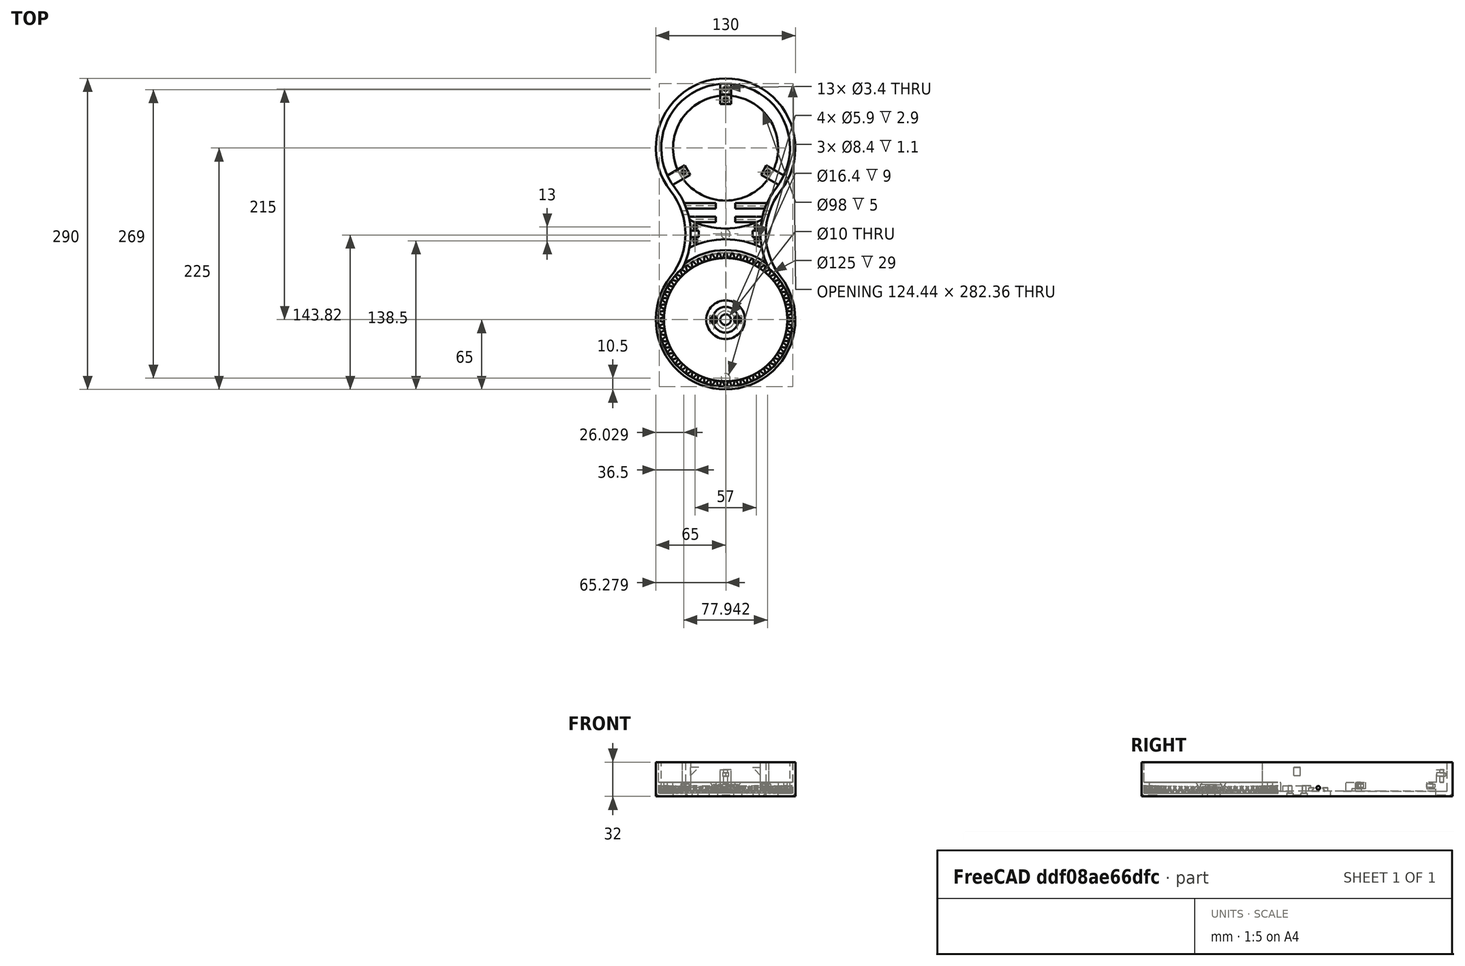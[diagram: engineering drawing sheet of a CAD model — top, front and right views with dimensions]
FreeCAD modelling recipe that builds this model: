
FCSTD DOCUMENT  (FreeCAD 0.19R24276 (Git))
Label: Art2BodyA
License: All rights reserved
LicenseURL: http://en.wikipedia.org/wiki/All_rights_reserved
objects: Sketcher::SketchObject×22, PartDesign::Pocket×15, PartDesign::Line×11, PartDesign::CoordinateSystem×10, PartDesign::Pad×7, PartDesign::Plane×4, PartDesign::Body×2, Spreadsheet::Sheet×1, Part::FeaturePython×1, Part::Cylinder×1, Part::Cut×1, Part::MultiFuse×1, PartDesign::FeatureBase×1, PartDesign::Chamfer×1, PartDesign::Mirrored×1, PartDesign::PolarPattern×1, PartDesign::Fillet×1
note: 104 computed .brp shape members not serialized (recipe doc carries the construction recipe); baked Part::Feature solids carry a one-line shape summary decoded from their .brp

FEATURE [Spreadsheet::Sheet] Spreadsheet
  cells = A2=M3BoltBodyRadius; B2(M3BoltBodyRadius)=1.7; A3=M3BoltHeadRadius; B3(M3BoltHeadRadius)=2.95; A4=M3NutCircumradius; B4(M3NutCircumradius)=3.35; A5=M3NutThickness; B5(M3NutThickness)=3; A6=Bearing655ZZBodyRadius; B6(Bearing655ZZBodyRadius)=8.199999999999999; A7=MagnetRadius; B7(MagnetRadius)=4.2; A8=MagnetThickness; B8(MagnetThickness)=1.1
FEATURE [Sketcher::SketchObject] Sketch
  FullyConstrained = true
  MapMode = 5
  Support = -> [XY_Plane]
  sketch-geometry (4):
    g0: ArcOfCircle CenterX=0 CenterY=0 CenterZ=0 NormalX=0 NormalY=0 NormalZ=1 AngleXU=0 Radius=65 StartAngle=2.47872 EndAngle=6.94606
    g1: ArcOfCircle CenterX=102.47 CenterY=80 CenterZ=0 NormalX=0 NormalY=0 NormalZ=1 AngleXU=0 Radius=65 StartAngle=2.47872 EndAngle=3.80447
    g2: ArcOfCircle CenterX=-102.47 CenterY=80 CenterZ=0 NormalX=0 NormalY=0 NormalZ=1 AngleXU=0 Radius=65 StartAngle=5.62031 EndAngle=6.94606
    g3: ArcOfCircle CenterX=2.8e-15 CenterY=160 CenterZ=0 NormalX=0 NormalY=0 NormalZ=1 AngleXU=0 Radius=65 StartAngle=5.62031 EndAngle=10.0877
  constraints (10):
    c: Coincident(g0,g-1)
    c: Tangent(g2,g0) = 1.5708
    c: Tangent(g1,g0) = 1.5708
    c: Symmetric(g1,g2,g-2)
    c: Tangent(g3,g1) = 1.5708
    c: Tangent(g3,g2) = 1.5708
    c: Equal(g3,g0)
    c: DistanceY(g0,g3) = 160
    c: Radius(g0) = 65
    c: Equal(g2,g0)
FEATURE [PartDesign::Pad] Pad
  Direction = (1,1,1)
  Length = 32
  Length2 = 100
  Profile = -> Sketch
  Refine = true
  Type = 0
FEATURE [Sketcher::SketchObject] Sketch001
  ExternalGeometry = -> [Pad]
  FullyConstrained = true
  MapMode = 5
  Placement = pos=(0,0,32) rot=(0,0,1;0rad)
  Support = -> [Pad]
  sketch-geometry (4):
    g0: ArcOfCircle CenterX=0 CenterY=0 CenterZ=0 NormalX=0 NormalY=0 NormalZ=1 AngleXU=0 Radius=60 StartAngle=2.47872 EndAngle=6.94606
    g1: ArcOfCircle CenterX=102.47 CenterY=80 CenterZ=0 NormalX=0 NormalY=0 NormalZ=1 AngleXU=0 Radius=70 StartAngle=2.47872 EndAngle=3.80447
    g2: ArcOfCircle CenterX=-102.47 CenterY=80 CenterZ=0 NormalX=0 NormalY=0 NormalZ=1 AngleXU=0 Radius=70 StartAngle=5.62031 EndAngle=6.94606
    g3: ArcOfCircle CenterX=2.7e-15 CenterY=160 CenterZ=0 NormalX=0 NormalY=0 NormalZ=1 AngleXU=0 Radius=60 StartAngle=5.62031 EndAngle=10.0877
  constraints (9):
    c: Coincident(g0,g-1)
    c: Coincident(g1,g-4)
    c: Coincident(g2,g-5)
    c: Coincident(g2,g0)
    c: Coincident(g3,g-3)
    c: Tangent(g3,g2) = 1.5708
    c: Radius(g3) = 60
    c: Tangent(g3,g1) = 1.5708
    c: Tangent(g1,g0) = 1.5708
FEATURE [PartDesign::Pocket] Pocket
  BaseFeature = -> Pad
  Length = 27
  Length2 = 100
  Profile = -> Sketch001
  Refine = true
  Type = 0
FEATURE [Part::FeaturePython] involutegear  # WARN: FeaturePython — macro-defined, semantics opaque (R4)
  Placement = pos=(0,0,3) rot=(0,0,1;0rad)
  backlash = 0
  beta = -32
  clearance = 0.25
  double_helix = false
  dw = 120
  head = 0
  height = 15.5
  module = 2
  numpoints = 6
  pressure_angle = 20
  properties_from_tool = false
  reversed_backlash = false
  shift = 0
  simple = false
  teeth = 60
  transverse_pitch = 6.28319
  undercut = false
  version = 0.0.3
FEATURE [Sketcher::SketchObject] Sketch003
  FullyConstrained = true
  MapMode = 5
  Placement = pos=(0,0,3) rot=(0,0,1;0rad)
  sketch-geometry (1):
    g0: Circle CenterX=0 CenterY=0 CenterZ=0 NormalX=0 NormalY=0 NormalZ=1 AngleXU=0 Radius=18
  constraints (2):
    c: Coincident(g0,g-1)
    c: Radius(g0) = 18
FEATURE [PartDesign::Plane] DatumPlane
  AttachmentOffset = pos=(0,0,9) rot=(0,0,1;0rad)
  Length = 315.452
  MapMode = 5
  Placement = pos=(9,-2e-15,2e-15) rot=(0.57735,0.57735,0.57735;2.0944rad)
  ResizeMode = 0
  Support = -> [YZ_Plane001]
  Width = 82.7027
FEATURE [PartDesign::CoordinateSystem] LCS_Art2BodyA
  AttacherType = Attacher::AttachEngine3D
FEATURE [Part::Cylinder] Cylinder
  Angle = 360
  AttacherType = Attacher::AttachEngine3D
  Height = 13
  Radius = 64.9
FEATURE [Sketcher::SketchObject] Sketch021
  FullyConstrained = true
  MapMode = 5
  Placement = pos=(0,0,32) rot=(0,0,1;0rad)
  Support = -> [Pocket]
  sketch-geometry (1):
    g0: Circle CenterX=0 CenterY=0 CenterZ=0 NormalX=0 NormalY=0 NormalZ=1 AngleXU=0 Radius=62.5
  constraints (2):
    c: Coincident(g0,g-1)
    c: Radius(g0) = 62.5
FEATURE [PartDesign::Pocket] Pocket014
  BaseFeature = -> Pocket
  Length = 29
  Length2 = 100
  Profile = -> Sketch021
  Refine = true
  Type = 0
FEATURE [PartDesign::Body] Body
  Group = -> [Sketch,Pad,Sketch001,Pocket,Sketch021,Pocket014]
  Origin = -> Origin
  Tip = -> Pocket014
FEATURE [PartDesign::Plane] DatumPlane003
  AttachmentOffset = pos=(0,0,-80) rot=(0,0,1;0rad)
  Length = 147.174
  MapMode = 5
  Placement = pos=(0,80,1.78e-14) rot=(1,0,0;1.5708rad)
  ResizeMode = 0
  Support = -> [XZ_Plane001]
  Width = 74.2136
FEATURE [Part::Cut] Cut
  Base = -> Cylinder
  Refine = true
  Tool = -> involutegear
FEATURE [Part::MultiFuse] Fusion
  Refine = true
  Shapes = -> [Cut,Pocket014]
FEATURE [PartDesign::FeatureBase] BaseFeature  label="Fusion001"
  BaseFeature = -> Fusion
FEATURE [PartDesign::Pad] Pad002
  BaseFeature = -> BaseFeature
  Direction = (1,1,1)
  Length = 8
  Length2 = 100
  Profile = -> Sketch003
  Refine = true
  Type = 0
FEATURE [PartDesign::Chamfer] Chamfer
  Angle = 45
  Base = -> Pad002 [Edge755]
  BaseFeature = -> Pad002
  ChamferType = 0
  FlipDirection = false
  Refine = true
  Size = 6
  Size2 = 1
  SupportTransform = false
FEATURE [Sketcher::SketchObject] Sketch004
  FullyConstrained = true
  MapMode = 5
  Placement = pos=(0,0,11) rot=(0,0,1;0rad)
  Support = -> [Chamfer]
  expr: Constraints[5] = Spreadsheet.M3BoltBodyRadius
  sketch-geometry (3):
    g0: Circle CenterX=0 CenterY=0 CenterZ=0 NormalX=0 NormalY=0 NormalZ=1 AngleXU=0 Radius=5
    g1: Circle CenterX=11 CenterY=0 CenterZ=0 NormalX=0 NormalY=0 NormalZ=1 AngleXU=0 Radius=1.7
    g2: Circle CenterX=-11 CenterY=0 CenterZ=0 NormalX=0 NormalY=0 NormalZ=1 AngleXU=0 Radius=1.7
  constraints (7):
    c: Coincident(g0,g-1)
    c: PointOnObject(g1,g-1)
    c: Symmetric(g2,g1,g-2)
    c: DistanceX(g2,g1) = 22
    c: Radius(g0) = 5
    c: Radius(g2) = 1.7
    c: Equal(g1,g2)
FEATURE [PartDesign::Pocket] Pocket001
  BaseFeature = -> Chamfer
  Length = 5
  Length2 = 100
  Profile = -> Sketch004
  Refine = true
  Type = 1
FEATURE [Sketcher::SketchObject] Sketch005
  FullyConstrained = true
  MapMode = 5
  Placement = pos=(0,0,0) rot=(1,0,0;3.14159rad)
  Support = -> [Pocket001]
  expr: Constraints[1] = Spreadsheet.Bearing655ZZBodyRadius
  sketch-geometry (1):
    g0: Circle CenterX=0 CenterY=0 CenterZ=0 NormalX=0 NormalY=0 NormalZ=1 AngleXU=0 Radius=8.2
  constraints (2):
    c: Coincident(g0,g-1)
    c: Radius(g0) = 8.2
FEATURE [PartDesign::Pocket] Pocket002
  BaseFeature = -> Pocket001
  Length = 9
  Length2 = 100
  Profile = -> Sketch005
  Refine = true
  Type = 0
FEATURE [Sketcher::SketchObject] Sketch006
  FullyConstrained = true
  MapMode = 5
  Placement = pos=(0,0,0) rot=(1,0,0;3.14159rad)
  Support = -> [Pocket002]
  sketch-geometry (4):
    g0: LineSegment StartX=-15.3 StartY=3.5 StartZ=0 EndX=15.3 EndY=3.5 EndZ=0
    g1: LineSegment StartX=15.3 StartY=3.5 StartZ=0 EndX=15.3 EndY=-3.5 EndZ=0
    g2: LineSegment StartX=15.3 StartY=-3.5 StartZ=0 EndX=-15.3 EndY=-3.5 EndZ=0
    g3: LineSegment StartX=-15.3 StartY=-3.5 StartZ=0 EndX=-15.3 EndY=3.5 EndZ=0
  constraints (10):
    c: Coincident(g0,g1)
    c: Coincident(g1,g2)
    c: Coincident(g2,g3)
    c: Coincident(g3,g0)
    c: Horizontal(g0)
    c: Vertical(g3)
    c: Symmetric(g0,g1,g-1)
    c: Symmetric(g2,g1,g-2)
    c: DistanceX(g2,g2) = 30.6
    c: DistanceY(g3,g3) = 7
FEATURE [PartDesign::Pocket] Pocket003
  BaseFeature = -> Pocket002
  Length = 4
  Length2 = 100
  Profile = -> Sketch006
  Refine = true
  Type = 0
FEATURE [Sketcher::SketchObject] Sketch007
  ExternalGeometry = -> [Pocket003]
  FullyConstrained = true
  MapMode = 5
  Placement = pos=(0,0,11) rot=(0,0,1;0rad)
  Support = -> [Pocket003]
  expr: Constraints[39] = Spreadsheet.M3NutCircumradius
  sketch-geometry (14):
    g0: LineSegment StartX=11 StartY=3.35 StartZ=0 EndX=8.09881 EndY=1.675 EndZ=0
    g1: LineSegment StartX=8.09881 StartY=1.675 StartZ=0 EndX=8.09881 EndY=-1.675 EndZ=0
    g2: LineSegment StartX=8.09881 StartY=-1.675 StartZ=0 EndX=11 EndY=-3.35 EndZ=0
    g3: LineSegment StartX=11 StartY=-3.35 StartZ=0 EndX=13.9012 EndY=-1.675 EndZ=0
    g4: LineSegment StartX=13.9012 StartY=-1.675 StartZ=0 EndX=13.9012 EndY=1.675 EndZ=0
    g5: LineSegment StartX=13.9012 StartY=1.675 StartZ=0 EndX=11 EndY=3.35 EndZ=0
    g6: Circle CenterX=11 CenterY=0 CenterZ=0 NormalX=0 NormalY=0 NormalZ=1 AngleXU=0 Radius=3.35
    g7: LineSegment StartX=-11 StartY=3.35 StartZ=0 EndX=-13.9012 EndY=1.675 EndZ=0
    g8: LineSegment StartX=-13.9012 StartY=1.675 StartZ=0 EndX=-13.9012 EndY=-1.675 EndZ=0
    g9: LineSegment StartX=-13.9012 StartY=-1.675 StartZ=0 EndX=-11 EndY=-3.35 EndZ=0
    g10: LineSegment StartX=-11 StartY=-3.35 StartZ=0 EndX=-8.09881 EndY=-1.675 EndZ=0
    g11: LineSegment StartX=-8.09881 StartY=-1.675 StartZ=0 EndX=-8.09881 EndY=1.675 EndZ=0
    g12: LineSegment StartX=-8.09881 StartY=1.675 StartZ=0 EndX=-11 EndY=3.35 EndZ=0
    g13: Circle CenterX=-11 CenterY=0 CenterZ=0 NormalX=0 NormalY=0 NormalZ=1 AngleXU=0 Radius=3.35
  constraints (32):
    c: Coincident(g0,g1)
    c: Coincident(g1,g2)
    c: Coincident(g2,g3)
    c: Coincident(g3,g4)
    c: Coincident(g4,g5)
    c: Coincident(g5,g0)
    c: Equal(g0, g1-g5) x5
    c: PointOnObject(g0,g6)
    c: PointOnObject(g1,g6)
    c: PointOnObject(g2,g6)
    c: PointOnObject(g3,g6)
    c: PointOnObject(g4,g6)
    c: PointOnObject(g5,g6)
    c: Coincident(g6,g-3)
    c: Coincident(g7,g8)
    c: Coincident(g8,g9)
    c: Coincident(g9,g10)
    c: Coincident(g10,g11)
    c: Coincident(g11,g12)
    c: Coincident(g12,g7)
    c: Equal(g7, g8-g12) x5
    c: PointOnObject(g7,g13)
    c: PointOnObject(g8,g13)
    c: PointOnObject(g9,g13)
    c: PointOnObject(g10,g13)
    c: PointOnObject(g11,g13)
    c: PointOnObject(g12,g13)
    c: Coincident(g13,g-4)
    c: Vertical(g11)
    c: Vertical(g1)
    c: Equal(g6,g13)
    c: Radius(g6) = 3.35
FEATURE [PartDesign::Pocket] Pocket004
  BaseFeature = -> Pocket003
  Length = 4
  Length2 = 100
  Profile = -> Sketch007
  Refine = true
  Type = 0
FEATURE [Sketcher::SketchObject] Sketch008
  ExternalGeometry = -> [Pocket004]
  FullyConstrained = true
  MapMode = 5
  Placement = pos=(0,0,0) rot=(1,0,0;3.14159rad)
  Support = -> [Pocket004]
  sketch-geometry (1):
    g0: Circle CenterX=0 CenterY=-160 CenterZ=0 NormalX=0 NormalY=0 NormalZ=1 AngleXU=0 Radius=49
  constraints (2):
    c: Radius(g0) = 49
    c: Coincident(g0,g-3)
FEATURE [PartDesign::Pocket] Pocket005
  BaseFeature = -> Pocket004
  Length = 5
  Length2 = 100
  Profile = -> Sketch008
  Refine = true
  Type = 0
FEATURE [Sketcher::SketchObject] Sketch009
  ExternalGeometry = -> [Pocket005]
  FullyConstrained = true
  MapMode = 5
  Placement = pos=(0,0,5) rot=(0,0,1;0rad)
  Support = -> [Pocket005]
  sketch-geometry (4):
    g0: ArcOfCircle CenterX=0 CenterY=0 CenterZ=0 NormalX=0 NormalY=0 NormalZ=1 AngleXU=0 Radius=75 StartAngle=1.10499 EndAngle=2.0366
    g1: ArcOfCircle CenterX=2.7e-15 CenterY=160 CenterZ=0 NormalX=0 NormalY=0 NormalZ=1 AngleXU=0 Radius=75 StartAngle=4.24659 EndAngle=5.17819
    g2: ArcOfCircle CenterX=102.47 CenterY=80 CenterZ=0 NormalX=0 NormalY=0 NormalZ=1 AngleXU=0 Radius=70 StartAngle=2.95493 EndAngle=3.32825
    g3: ArcOfCircle CenterX=-102.47 CenterY=80 CenterZ=0 NormalX=0 NormalY=0 NormalZ=1 AngleXU=0 Radius=70 StartAngle=6.09653 EndAngle=6.46984
  constraints (12):
    c: Coincident(g0,g-1)
    c: Radius(g0) = 75
    c: Coincident(g2,g1)
    c: Coincident(g2,g0)
    c: Coincident(g3,g1)
    c: Coincident(g3,g0)
    c: Equal(g1,g0)
    c: Coincident(g1,g-3)
    c: Equal(g3,g2)
    c: Coincident(g2,g-4)
    c: Coincident(g3,g-5)
    c: Equal(g3,g-5)
FEATURE [PartDesign::Pad] Pad003
  BaseFeature = -> Pocket005
  Direction = (1,1,1)
  Length = 5
  Length2 = 100
  Profile = -> Sketch009
  Refine = true
  Type = 0
FEATURE [Sketcher::SketchObject] Sketch010
  ExternalGeometry = -> [Pad003]
  FullyConstrained = true
  MapMode = 5
  Placement = pos=(9,-2e-15,2e-15) rot=(0.57735,0.57735,0.57735;2.0944rad)
  Support = -> [DatumPlane]
  sketch-geometry (8):
    g0: LineSegment StartX=91 StartY=8.03897 StartZ=0 EndX=96 EndY=8.03897 EndZ=0
    g1: LineSegment StartX=96 StartY=8.03897 StartZ=0 EndX=93.45 EndY=5 EndZ=0
    g2: LineSegment StartX=93.45 StartY=5 StartZ=0 EndX=91 EndY=5 EndZ=0
    g3: LineSegment StartX=91 StartY=5 StartZ=0 EndX=91 EndY=8.03897 EndZ=0
    g4: LineSegment StartX=103.7 StartY=8.03897 StartZ=0 EndX=108.7 EndY=8.03897 EndZ=0
    g5: LineSegment StartX=108.7 StartY=8.03897 StartZ=0 EndX=108.7 EndY=5 EndZ=0
    g6: LineSegment StartX=108.7 StartY=5 StartZ=0 EndX=106.25 EndY=5 EndZ=0
    g7: LineSegment StartX=106.25 StartY=5 StartZ=0 EndX=103.7 EndY=8.03897 EndZ=0
  constraints (24):
    c: Horizontal(g0)
    c: Coincident(g0,g1)
    c: PointOnObject(g1,g-3)
    c: Coincident(g1,g2)
    c: Horizontal(g2)
    c: Coincident(g2,g3)
    c: Vertical(g3)
    c: Coincident(g0,g3)
    c: Horizontal(g4)
    c: Coincident(g4,g5)
    c: Vertical(g5)
    c: Coincident(g5,g6)
    c: Horizontal(g6)
    c: Coincident(g6,g7)
    c: Coincident(g7,g4)
    c: Equal(g1,g7)
    c: Equal(g5,g3)
    c: Equal(g4,g0)
    c: PointOnObject(g6,g-3)
    c: DistanceX(g1,g6) = 12.8
    c: DistanceX(g0,g4) = 7.7
    c: Angle(g-3,g1) = 0.872665
    c: DistanceX(g0,g0) = 5
    c: DistanceX(g-1,g2) = 91
FEATURE [PartDesign::Pad] Pad004
  BaseFeature = -> Pad003
  Direction = (1,1,1)
  Length = 10
  Length2 = 100
  Profile = -> Sketch010
  Refine = true
  Type = 3
  UpToFace = -> Pad003 [Face265]
FEATURE [PartDesign::Mirrored] Mirrored
  BaseFeature = -> Pad004
  MirrorPlane = -> YZ_Plane001
  Originals = -> [Pad004]
  Refine = true
FEATURE [Sketcher::SketchObject] Sketch011
  ExternalGeometry = -> [Mirrored]
  FullyConstrained = true
  MapMode = 5
  Placement = pos=(0,0,0) rot=(0.57735,0.57735,0.57735;2.0944rad)
  Support = -> [YZ_Plane001]
  sketch-geometry (6):
    g0: LineSegment StartX=221 StartY=5 StartZ=0 EndX=221 EndY=13 EndZ=0
    g1: LineSegment StartX=221 StartY=13 StartZ=0 EndX=201 EndY=13 EndZ=0
    g2: LineSegment StartX=201 StartY=13 StartZ=0 EndX=201 EndY=7 EndZ=0
    g3: LineSegment StartX=201 StartY=7 StartZ=0 EndX=209 EndY=7 EndZ=0
    g4: LineSegment StartX=209 StartY=7 StartZ=0 EndX=209 EndY=5 EndZ=0
    g5: LineSegment StartX=209 StartY=5 StartZ=0 EndX=221 EndY=5 EndZ=0
  constraints (17):
    c: Vertical(g0)
    c: Coincident(g0,g1)
    c: Coincident(g1,g2)
    c: Coincident(g2,g3)
    c: Coincident(g3,g4)
    c: Coincident(g4,g5)
    c: Coincident(g5,g0)
    c: Horizontal(g5)
    c: Vertical(g4)
    c: Vertical(g2)
    c: Horizontal(g3)
    c: Horizontal(g1)
    c: DistanceX(g3,g3) = 8
    c: DistanceX(g1,g1) = 20
    c: DistanceY(g2,g2) = 6
    c: DistanceY(g4,g4) = 2
    c: Coincident(g4,g-3)
FEATURE [PartDesign::Pad] Pad005
  BaseFeature = -> Mirrored
  Direction = (1,1,1)
  Length = 10
  Length2 = 100
  Midplane = true
  Profile = -> Sketch011
  Refine = true
  Type = 0
FEATURE [Sketcher::SketchObject] Sketch012
  ExternalGeometry = -> [Pad005]
  FullyConstrained = false
  MapMode = 5
  Placement = pos=(-3.6e-15,2.9e-15,13) rot=(0,0,1;0rad)
  Support = -> [Pad005]
  expr: Constraints[1] = Spreadsheet.M3BoltBodyRadius
  sketch-geometry (1):
    g0: Circle CenterX=0 CenterY=205 CenterZ=0 NormalX=0 NormalY=0 NormalZ=1 AngleXU=0 Radius=1.7
  constraints (2):
    c: PointOnObject(g0,g-2)
    c: Radius(g0) = 1.7
FEATURE [PartDesign::Pocket] Pocket006
  BaseFeature = -> Pad005
  Length = 5
  Length2 = 100
  Profile = -> Sketch012
  Refine = true
  Type = 1
FEATURE [PartDesign::Plane] DatumPlane001
  AttachmentOffset = pos=(0,0,-3) rot=(0,0,1;0rad)
  Length = 168.771
  MapMode = 5
  Placement = pos=(-2.8e-15,2.2e-15,10) rot=(0,0,1;0rad)
  ResizeMode = 0
  Support = -> [Pocket006]
  Width = 328.56
FEATURE [Sketcher::SketchObject] Sketch013
  ExternalGeometry = -> [Pocket006]
  FullyConstrained = true
  MapMode = 5
  Placement = pos=(-2.8e-15,2.2e-15,10) rot=(0,0,1;0rad)
  Support = -> [DatumPlane001]
  expr: Constraints[18] = Spreadsheet.M3NutCircumradius
  sketch-geometry (10):
    g0: LineSegment StartX=0 StartY=208.35 StartZ=0 EndX=-2.90119 EndY=206.675 EndZ=0
    g1: LineSegment StartX=-2.90119 StartY=206.675 StartZ=0 EndX=-2.90119 EndY=203.325 EndZ=0
    g2: LineSegment StartX=-2.90119 StartY=203.325 StartZ=0 EndX=-9.28e-14 EndY=201.65 EndZ=0
    g3: LineSegment StartX=-9.28e-14 StartY=201.65 StartZ=0 EndX=2.90119 EndY=203.325 EndZ=0
    g4: LineSegment StartX=2.90119 StartY=203.325 StartZ=0 EndX=2.90119 EndY=206.675 EndZ=0
    g5: LineSegment StartX=2.90119 StartY=206.675 StartZ=0 EndX=0 EndY=208.35 EndZ=0
    g6: Circle CenterX=0 CenterY=205 CenterZ=0 NormalX=0 NormalY=0 NormalZ=1 AngleXU=0 Radius=3.35
    g7: LineSegment StartX=-2.90119 StartY=206.675 StartZ=0 EndX=-2.90119 EndY=196.675 EndZ=0
    g8: LineSegment StartX=-2.90119 StartY=196.675 StartZ=0 EndX=2.90119 EndY=196.675 EndZ=0
    g9: LineSegment StartX=2.90119 StartY=196.675 StartZ=0 EndX=2.90119 EndY=206.675 EndZ=0
  constraints (24):
    c: Coincident(g0,g1)
    c: Coincident(g1,g2)
    c: Coincident(g2,g3)
    c: Coincident(g3,g4)
    c: Coincident(g4,g5)
    c: Coincident(g5,g0)
    c: Equal(g0, g1-g5) x5
    c: PointOnObject(g0,g6)
    c: PointOnObject(g1,g6)
    c: PointOnObject(g2,g6)
    c: PointOnObject(g3,g6)
    c: PointOnObject(g4,g6)
    c: PointOnObject(g5,g6)
    c: PointOnObject(g5,g-2)
    c: Radius(g6) = 3.35
    c: Coincident(g0,g7)
    c: Vertical(g7)
    c: Coincident(g7,g8)
    c: Horizontal(g8)
    c: Coincident(g8,g9)
    c: Coincident(g9,g5)
    c: Vertical(g9)
    c: DistanceY(g9,g9) = 10
    c: Coincident(g6,g-3)
FEATURE [PartDesign::Pocket] Pocket007
  BaseFeature = -> Pocket006
  Length = 3
  Length2 = 100
  Midplane = true
  Profile = -> Sketch013
  Refine = true
  Type = 0
  expr: Length = Spreadsheet.M3NutThickness
FEATURE [PartDesign::Line] DatumLine
  AttacherType = Attacher::AttachEngineLine
  Length = 20
  MapMode = 19
  Placement = pos=(-7.1e-15,160,0) rot=(-1,0,0;3.14159rad)
  ResizeMode = 0
  Support = -> [Pocket007]
FEATURE [PartDesign::PolarPattern] PolarPattern
  Angle = 360
  Axis = -> DatumLine
  BaseFeature = -> Pocket007
  Occurrences = 3
  Originals = -> [Pad005,Pocket006,Pocket007]
  Refine = true
FEATURE [Sketcher::SketchObject] Sketch014
  ExternalGeometry = -> [PolarPattern]
  FullyConstrained = true
  MapMode = 5
  Placement = pos=(-3.6e-15,2.9e-15,13) rot=(0,0,1;0rad)
  Support = -> [PolarPattern]
  sketch-geometry (4):
    g0: LineSegment StartX=-5 StartY=219.791 StartZ=0 EndX=-5 EndY=210 EndZ=0
    g1: LineSegment StartX=-5 StartY=210 StartZ=0 EndX=5 EndY=210 EndZ=0
    g2: LineSegment StartX=5 StartY=210 StartZ=0 EndX=5 EndY=219.791 EndZ=0
    g3: ArcOfCircle CenterX=1.16e-14 CenterY=160 CenterZ=0 NormalX=0 NormalY=0 NormalZ=1 AngleXU=0 Radius=60 StartAngle=1.48737 EndAngle=1.65423
  constraints (11):
    c: Vertical(g0)
    c: Coincident(g0,g1)
    c: Coincident(g1,g2)
    c: Vertical(g2)
    c: Symmetric(g1,g0,g-2)
    c: Coincident(g3,g0)
    c: Coincident(g3,g2)
    c: DistanceY(g-4,g1) = 9
    c: Coincident(g3,g-3)
    c: Equal(g-3,g3)
    c: DistanceX(g1,g1) = 10
FEATURE [PartDesign::Pad] Pad006
  BaseFeature = -> PolarPattern
  Direction = (1,1,1)
  Length = 12
  Length2 = 100
  Profile = -> Sketch014
  Refine = true
  Type = 0
FEATURE [Sketcher::SketchObject] Sketch015
  ExternalGeometry = -> [Pad006]
  FullyConstrained = true
  MapMode = 5
  Placement = pos=(-7.3e-15,6.8e-15,25) rot=(0,0,1;0rad)
  Support = -> [Pad006]
  expr: Constraints[1] = Spreadsheet.M3BoltBodyRadius
  sketch-geometry (1):
    g0: Circle CenterX=0 CenterY=215 CenterZ=0 NormalX=0 NormalY=0 NormalZ=1 AngleXU=0 Radius=1.7
  constraints (3):
    c: DistanceY(g-3,g0) = 5
    c: Radius(g0) = 1.7
    c: PointOnObject(g0,g-2)
FEATURE [PartDesign::Pocket] Pocket008
  BaseFeature = -> Pad006
  Length = 12
  Length2 = 100
  Profile = -> Sketch015
  Refine = true
  Type = 0
FEATURE [PartDesign::Plane] DatumPlane002
  AttachmentOffset = pos=(0,0,-4.5) rot=(0,0,1;0rad)
  Length = 168.771
  MapMode = 5
  Placement = pos=(-5.9e-15,5.5e-15,20.5) rot=(0,0,1;0rad)
  ResizeMode = 0
  Support = -> [Pocket008]
  Width = 328.56
FEATURE [Sketcher::SketchObject] Sketch016
  ExternalGeometry = -> [Pocket008]
  FullyConstrained = true
  MapMode = 5
  Placement = pos=(-5.9e-15,5.5e-15,20.5) rot=(0,0,1;0rad)
  Support = -> [DatumPlane002]
  expr: Constraints[18] = Spreadsheet.M3NutCircumradius
  sketch-geometry (10):
    g0: LineSegment StartX=0 StartY=211.65 StartZ=0 EndX=2.90119 EndY=213.325 EndZ=0
    g1: LineSegment StartX=2.90119 StartY=213.325 StartZ=0 EndX=2.90119 EndY=216.675 EndZ=0
    g2: LineSegment StartX=2.90119 StartY=216.675 StartZ=0 EndX=6.2e-15 EndY=218.35 EndZ=0
    g3: LineSegment StartX=6.2e-15 StartY=218.35 StartZ=0 EndX=-2.90119 EndY=216.675 EndZ=0
    g4: LineSegment StartX=-2.90119 StartY=216.675 StartZ=0 EndX=-2.90119 EndY=213.325 EndZ=0
    g5: LineSegment StartX=-2.90119 StartY=213.325 StartZ=0 EndX=0 EndY=211.65 EndZ=0
    g6: Circle CenterX=0 CenterY=215 CenterZ=0 NormalX=0 NormalY=0 NormalZ=1 AngleXU=0 Radius=3.35
    g7: LineSegment StartX=2.90119 StartY=216.675 StartZ=0 EndX=2.90119 EndY=206.675 EndZ=0
    g8: LineSegment StartX=2.90119 StartY=206.675 StartZ=0 EndX=-2.90119 EndY=206.675 EndZ=0
    g9: LineSegment StartX=-2.90119 StartY=206.675 StartZ=0 EndX=-2.90119 EndY=216.675 EndZ=0
  constraints (24):
    c: Coincident(g0,g1)
    c: Coincident(g1,g2)
    c: Coincident(g2,g3)
    c: Coincident(g3,g4)
    c: Coincident(g4,g5)
    c: Coincident(g5,g0)
    c: Equal(g0, g1-g5) x5
    c: PointOnObject(g0,g6)
    c: PointOnObject(g1,g6)
    c: PointOnObject(g2,g6)
    c: PointOnObject(g3,g6)
    c: PointOnObject(g4,g6)
    c: PointOnObject(g5,g6)
    c: PointOnObject(g5,g-2)
    c: Radius(g6) = 3.35
    c: Vertical(g7)
    c: Coincident(g7,g8)
    c: Coincident(g8,g9)
    c: Vertical(g9)
    c: Horizontal(g8)
    c: Coincident(g7,g1)
    c: Coincident(g9,g3)
    c: Coincident(g6,g-3)
    c: DistanceY(g7,g7) = 10
FEATURE [PartDesign::Pocket] Pocket009
  BaseFeature = -> Pocket008
  Length = 3
  Length2 = 100
  Midplane = true
  Profile = -> Sketch016
  Refine = true
  Type = 0
  expr: Length = Spreadsheet.M3NutThickness
FEATURE [Sketcher::SketchObject] Sketch017
  ExternalGeometry = -> [Pocket009]
  FullyConstrained = true
  MapMode = 5
  Placement = pos=(0,0,0) rot=(0.57735,0.57735,0.57735;2.0944rad)
  Support = -> [YZ_Plane001]
  expr: Constraints[0] = Spreadsheet.M3BoltBodyRadius
  sketch-geometry (3):
    g0: Circle CenterX=99.85 CenterY=8 CenterZ=0 NormalX=0 NormalY=0 NormalZ=1 AngleXU=0 Radius=1.7
    g1: LineSegment StartX=93.45 StartY=5 StartZ=0 EndX=99.85 EndY=8 EndZ=0
    g2: LineSegment StartX=99.85 StartY=8 StartZ=0 EndX=106.25 EndY=5 EndZ=0
  constraints (7):
    c: Radius(g0) = 1.7
    c: Coincident(g1,g-3)
    c: Coincident(g1,g0)
    c: Coincident(g2,g-4)
    c: Coincident(g0,g2)
    c: Equal(g2,g1)
    c: DistanceY(g1,g0) = 3
FEATURE [PartDesign::Pocket] Pocket010
  BaseFeature = -> Pocket009
  Length = 5
  Length2 = 100
  Midplane = true
  Profile = -> Sketch017
  Refine = true
  Type = 1
FEATURE [Sketcher::SketchObject] Sketch018
  FullyConstrained = true
  MapMode = 5
  Placement = pos=(0,0,0) rot=(1,0,0;3.14159rad)
  Support = -> [Pocket010]
  expr: Constraints[14] = Spreadsheet.M3BoltBodyRadius
  sketch-geometry (8):
    g0: Circle CenterX=-28.5 CenterY=-73.5 CenterZ=0 NormalX=0 NormalY=0 NormalZ=1 AngleXU=0 Radius=1.7
    g1: LineSegment StartX=-28.5 StartY=-73.5 StartZ=0 EndX=28.5 EndY=-73.5 EndZ=0
    g2: LineSegment StartX=28.5 StartY=-73.5 StartZ=0 EndX=28.5 EndY=-86.5 EndZ=0
    g3: LineSegment StartX=28.5 StartY=-86.5 StartZ=0 EndX=-28.5 EndY=-86.5 EndZ=0
    g4: LineSegment StartX=-28.5 StartY=-86.5 StartZ=0 EndX=-28.5 EndY=-73.5 EndZ=0
    g5: Circle CenterX=28.5 CenterY=-73.5 CenterZ=0 NormalX=0 NormalY=0 NormalZ=1 AngleXU=0 Radius=1.7
    g6: Circle CenterX=28.5 CenterY=-86.5 CenterZ=0 NormalX=0 NormalY=0 NormalZ=1 AngleXU=0 Radius=1.7
    g7: Circle CenterX=-28.5 CenterY=-86.5 CenterZ=0 NormalX=0 NormalY=0 NormalZ=1 AngleXU=0 Radius=1.7
  constraints (19):
    c: Coincident(g1,g2)
    c: Coincident(g2,g3)
    c: Coincident(g3,g4)
    c: Coincident(g4,g1)
    c: Horizontal(g1)
    c: Vertical(g2)
    c: Vertical(g4)
    c: Coincident(g1,g0)
    c: Coincident(g5,g1)
    c: Coincident(g6,g2)
    c: Coincident(g7,g3)
    c: Equal(g7,g0)
    c: Equal(g0,g5)
    c: Equal(g5,g6)
    c: Radius(g6) = 1.7
    c: Symmetric(g7,g6,g-2)
    c: DistanceY(g4,g4) = 13
    c: DistanceY(g0,g-1) = 73.5
    c: DistanceX(g3,g3) = 57
FEATURE [PartDesign::Pocket] Pocket011
  BaseFeature = -> Pocket010
  Length = 5
  Length2 = 100
  Profile = -> Sketch018
  Refine = true
  Type = 1
FEATURE [Sketcher::SketchObject] Sketch019
  ExternalGeometry = -> [Pocket011]
  FullyConstrained = true
  MapMode = 5
  Placement = pos=(0,0,0) rot=(1,0,0;3.14159rad)
  Support = -> [Pocket011]
  expr: Constraints[1] = Spreadsheet.M3BoltHeadRadius
  sketch-geometry (4):
    g0: Circle CenterX=-28.5 CenterY=-73.5 CenterZ=0 NormalX=0 NormalY=0 NormalZ=1 AngleXU=0 Radius=2.95
    g1: Circle CenterX=-28.5 CenterY=-86.5 CenterZ=0 NormalX=0 NormalY=0 NormalZ=1 AngleXU=0 Radius=2.95
    g2: Circle CenterX=28.5 CenterY=-73.5 CenterZ=0 NormalX=0 NormalY=0 NormalZ=1 AngleXU=0 Radius=2.95
    g3: Circle CenterX=28.5 CenterY=-86.5 CenterZ=0 NormalX=0 NormalY=0 NormalZ=1 AngleXU=0 Radius=2.95
  constraints (8):
    c: Coincident(g0,g-3)
    c: Radius(g0) = 2.95
    c: Equal(g1,g0)
    c: Coincident(g1,g-4)
    c: Coincident(g2,g-5)
    c: Coincident(g3,g-6)
    c: Equal(g3,g2)
    c: Equal(g2,g0)
FEATURE [PartDesign::Pocket] Pocket012
  BaseFeature = -> Pocket011
  Length = 2.9
  Length2 = 100
  Profile = -> Sketch019
  Refine = true
  Type = 0
FEATURE [PartDesign::Fillet] Fillet
  Base = -> Pocket012 [Edge845,Edge848]
  BaseFeature = -> Pocket012
  Radius = 5
  Refine = true
  SupportTransform = false
FEATURE [Sketcher::SketchObject] Sketch020
  FullyConstrained = true
  MapMode = 5
  Placement = pos=(0,0,0) rot=(1,0,0;3.14159rad)
  Support = -> [Fillet]
  expr: Constraints[8] = Spreadsheet.MagnetRadius
  sketch-geometry (3):
    g0: Circle CenterX=0 CenterY=54.5 CenterZ=0 NormalX=0 NormalY=0 NormalZ=1 AngleXU=0 Radius=4.2
    g1: Circle CenterX=0 CenterY=-80 CenterZ=0 NormalX=0 NormalY=0 NormalZ=1 AngleXU=0 Radius=4.2
    g2: Circle CenterX=0 CenterY=-214.5 CenterZ=0 NormalX=0 NormalY=0 NormalZ=1 AngleXU=0 Radius=4.2
  constraints (9):
    c: PointOnObject(g0,g-2)
    c: PointOnObject(g1,g-2)
    c: PointOnObject(g2,g-2)
    c: DistanceY(g-1,g0) = 54.5
    c: DistanceY(g1,g-1) = 80
    c: DistanceY(g2,g1) = 134.5
    c: Equal(g2,g1)
    c: Equal(g1,g0)
    c: Radius(g2) = 4.2
FEATURE [PartDesign::Pocket] Pocket013
  BaseFeature = -> Fillet
  Length = 1.1
  Length2 = 100
  Profile = -> Sketch020
  Refine = true
  Type = 0
  expr: Length = Spreadsheet.MagnetThickness
FEATURE [PartDesign::CoordinateSystem] LCS_Bearing
  AttacherType = Attacher::AttachEngine3D
  MapMode = 11
  Placement = pos=(0,0,9) rot=(0,0,1;1.5708rad)
  Support = -> [Pocket013]
FEATURE [PartDesign::CoordinateSystem] LCS_Window
  AttacherType = Attacher::AttachEngine3D
  MapMode = 11
  Placement = pos=(-7.1e-15,160,0) rot=(0.707107,-0.707107,0;3.14159rad)
  Support = -> [Pocket013]
FEATURE [PartDesign::CoordinateSystem] LCS_Magnet2  label="LCS_Magnet"
  AttacherType = Attacher::AttachEngine3D
  MapMode = 11
  Placement = pos=(0,214.5,1.1) rot=(0.707107,-0.707107,0;3.14159rad)
  Support = -> [Pocket013]
FEATURE [PartDesign::CoordinateSystem] LCS_Magnet1
  AttacherType = Attacher::AttachEngine3D
  MapMode = 11
  Placement = pos=(0,80,1.1) rot=(0.707107,-0.707107,0;3.14159rad)
  Support = -> [Pocket013]
FEATURE [PartDesign::CoordinateSystem] LCS_Magnet2001  label="LCS_Magnet2"
  AttacherType = Attacher::AttachEngine3D
  MapMode = 11
  Placement = pos=(0,-54.5,1.1) rot=(0.707107,-0.707107,0;3.14159rad)
  Support = -> [Pocket013]
FEATURE [PartDesign::CoordinateSystem] LCS_Tensioner001
  AttacherType = Attacher::AttachEngine3D
  MapMode = 45
  Placement = pos=(-9,99.85,5) rot=(0,0.707107,0.707107;3.14159rad)
  Support = -> [Pocket013]
FEATURE [PartDesign::CoordinateSystem] LCS_Tensioner1
  AttacherType = Attacher::AttachEngine3D
  MapMode = 45
  Placement = pos=(9,99.85,5) rot=(0,0.707107,0.707107;3.14159rad)
  Support = -> [Pocket013]
FEATURE [PartDesign::CoordinateSystem] LCS_BearingFix
  AttacherType = Attacher::AttachEngine3D
  MapMode = 45
  Placement = pos=(9.3e-15,0,4) rot=(0,0,1;1.5708rad)
  Support = -> [Pocket013]
FEATURE [PartDesign::Line] HoleAxis_1
  AttacherType = Attacher::AttachEngineLine
  Length = 4.79083
  MapMode = 19
  Placement = pos=(-3.1e-15,205,11.5) rot=(0,0,1;0rad)
  ResizeMode = 1
  Support = -> [Pocket013]
FEATURE [PartDesign::Line] HoleAxis_2
  AttacherType = Attacher::AttachEngineLine
  Length = 4.79083
  MapMode = 19
  Placement = pos=(-6.4e-15,215,22) rot=(0,0,1;0rad)
  ResizeMode = 1
  Support = -> [Pocket013]
FEATURE [PartDesign::Line] HoleAxis_3
  AttacherType = Attacher::AttachEngineLine
  Length = 4.79858
  MapMode = 19
  Placement = pos=(-38.9711,137.5,11.5) rot=(0,0,1;2.0944rad)
  ResizeMode = 1
  Support = -> [Pocket013]
FEATURE [PartDesign::Line] HoleAxis_4
  AttacherType = Attacher::AttachEngineLine
  Length = 4.79858
  MapMode = 19
  Placement = pos=(38.9711,137.5,11.5) rot=(0,0,1;4.18879rad)
  ResizeMode = 1
  Support = -> [Pocket013]
FEATURE [PartDesign::Line] HoleAxis_5
  AttacherType = Attacher::AttachEngineLine
  Length = 4.79083
  MapMode = 19
  Placement = pos=(-28.5,86.5,2.9) rot=(-1,0,0;3.14159rad)
  ResizeMode = 1
  Support = -> [Pocket013]
FEATURE [PartDesign::Line] HoleAxis_6
  AttacherType = Attacher::AttachEngineLine
  Length = 4.79083
  MapMode = 19
  Placement = pos=(-28.5,73.5,2.9) rot=(-1,0,0;3.14159rad)
  ResizeMode = 1
  Support = -> [Pocket013]
FEATURE [PartDesign::Line] HoleAxis_7
  AttacherType = Attacher::AttachEngineLine
  Length = 4.79083
  MapMode = 19
  Placement = pos=(28.5,73.5,2.9) rot=(-1,0,0;3.14159rad)
  ResizeMode = 1
  Support = -> [Pocket013]
FEATURE [PartDesign::Line] HoleAxis_8
  AttacherType = Attacher::AttachEngineLine
  Length = 4.79083
  MapMode = 19
  Placement = pos=(28.5,86.5,2.9) rot=(-1,0,0;3.14159rad)
  ResizeMode = 1
  Support = -> [Pocket013]
FEATURE [PartDesign::Line] HoleAxis_9
  AttacherType = Attacher::AttachEngineLine
  Length = 4.79083
  MapMode = 19
  Placement = pos=(11,0,7) rot=(0,0,1;0rad)
  ResizeMode = 1
  Support = -> [Pocket013]
FEATURE [PartDesign::Line] HoleAxis_10
  AttacherType = Attacher::AttachEngineLine
  Length = 4.79083
  MapMode = 19
  Placement = pos=(-11,0,7) rot=(0,0,1;0rad)
  ResizeMode = 1
  Support = -> [Pocket013]
FEATURE [PartDesign::CoordinateSystem] LCS_Cover
  AttacherType = Attacher::AttachEngine3D
  AttachmentOffset = pos=(0,0,-32) rot=(0,0,1;0rad)
  MapMode = 11
  Placement = pos=(-7.1e-15,160,32) rot=(0.707107,-0.707107,0;3.14159rad)
  Support = -> [Pocket013]
FEATURE [Sketcher::SketchObject] Sketch022
  ExternalGeometry = -> [Pocket013]
  FullyConstrained = true
  MapMode = 5
  Placement = pos=(0,80,1.78e-14) rot=(1,0,0;1.5708rad)
  Support = -> [DatumPlane003]
  sketch-geometry (6):
    g0: LineSegment StartX=-25 StartY=27 StartZ=0 EndX=-35 EndY=27 EndZ=0
    g1: LineSegment StartX=-35 StartY=27 StartZ=0 EndX=-35 EndY=17 EndZ=0
    g2: LineSegment StartX=-35 StartY=17 StartZ=0 EndX=-25 EndY=27 EndZ=0
    g3: LineSegment StartX=25 StartY=27 StartZ=0 EndX=35 EndY=27 EndZ=0
    g4: LineSegment StartX=35 StartY=27 StartZ=0 EndX=35 EndY=17 EndZ=0
    g5: LineSegment StartX=35 StartY=17 StartZ=0 EndX=25 EndY=27 EndZ=0
  constraints (15):
    c: Horizontal(g0)
    c: Coincident(g0,g1)
    c: Vertical(g1)
    c: Coincident(g1,g2)
    c: Coincident(g2,g0)
    c: Coincident(g3,g4)
    c: Coincident(g4,g5)
    c: Coincident(g5,g3)
    c: Symmetric(g3,g0,g-2)
    c: Symmetric(g0,g3,g-2)
    c: Symmetric(g4,g1,g-2)
    c: DistanceX(g0,g3) = 50
    c: DistanceX(g0,g0) = 10
    c: Angle(g0,g2) = 0.785398
    c: DistanceY(g0,g-3) = 5
FEATURE [PartDesign::Pad] Pad007
  BaseFeature = -> Pocket013
  Direction = (1,1,1)
  Length = 6
  Length2 = 100
  Midplane = true
  Profile = -> Sketch022
  Refine = true
  Type = 0
FEATURE [PartDesign::Body] Body001  label="Art2BodyA"
  BaseFeature = -> Fusion
  Group = -> [BaseFeature,Sketch003,Pad002,Chamfer,Sketch004,Pocket001,Sketch005,Pocket002,Sketch006,Pocket003,Sketch007,Pocket004,Sketch008,Pocket005,Sketch009,Pad003,DatumPlane,Sketch010,Pad004,Mirrored,Sketch011,Pad005,Sketch012,Pocket006,DatumPlane001,Sketch013,Pocket007,DatumLine,PolarPattern,Sketch014,Pad006,Sketch015,Pocket008,DatumPlane002,Sketch016,Pocket009,Sketch017,Pocket010,Sketch018,Pocket011,+28 more]
  Origin = -> Origin001
  Tip = -> Pad007
